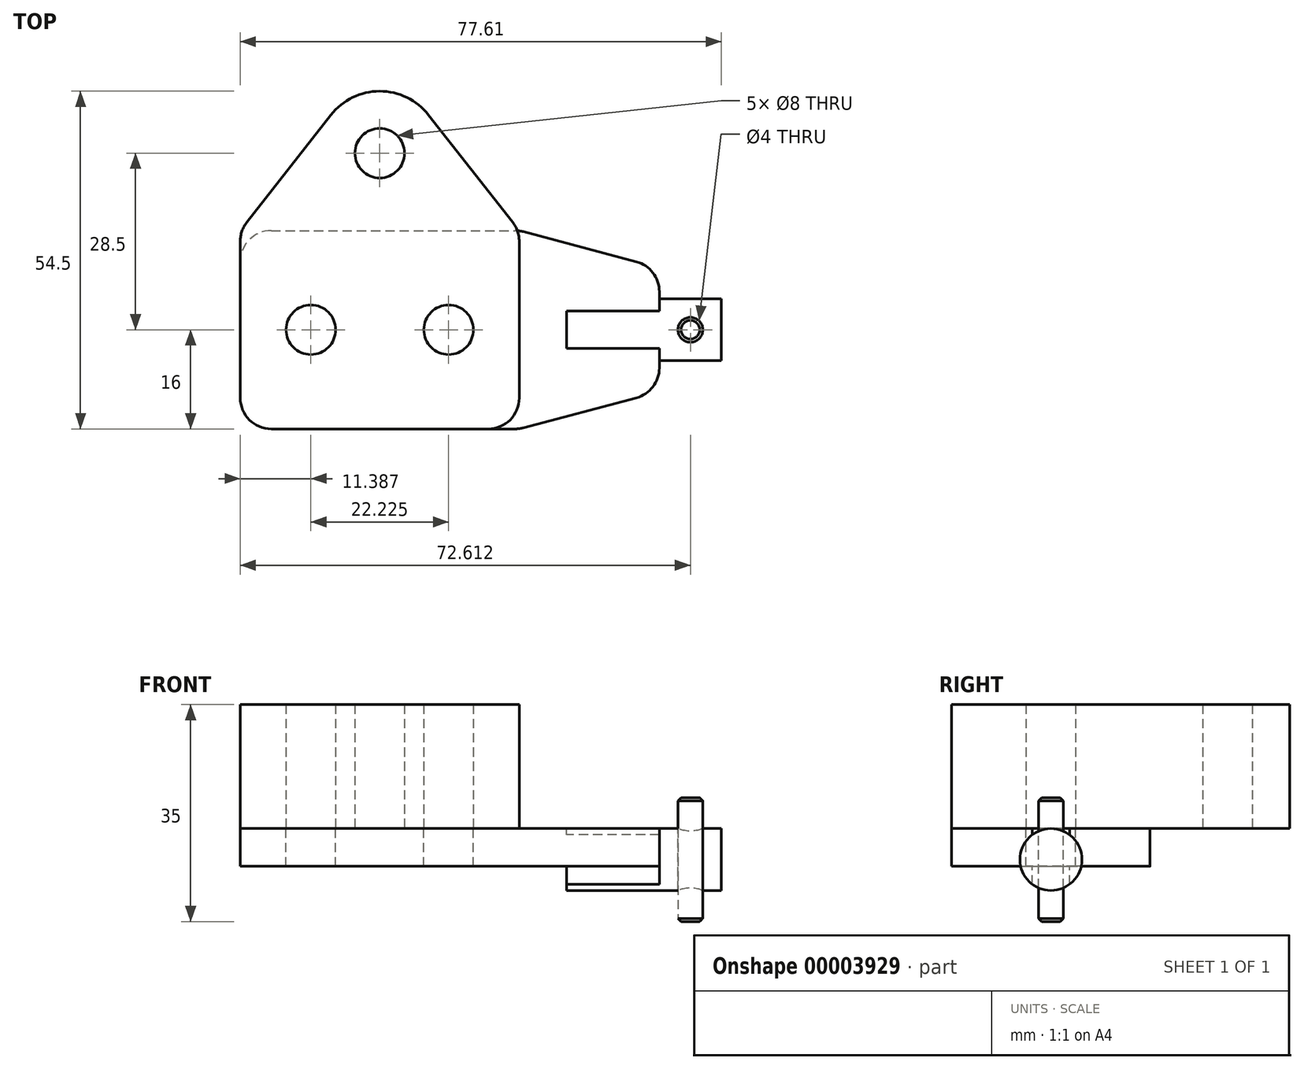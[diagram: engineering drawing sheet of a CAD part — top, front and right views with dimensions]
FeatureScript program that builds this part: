
annotation { "Feature Type Name" : "Feature", "Feature Type Description" : "" }
export const myFeature = defineFeature(function(context is Context, id is Id, definition is map)
    precondition{}
    {
        {
            var Q0;
            Q0=qCreatedBy(makeId("Top.planeOp"),FACE);
            var sketch = newSketch(context, id + "F0", { "sketchPlane" : qUnion([Q0])});
            skCircle(sketch, "E0", {"center": v(-11.11, 0) * mm, "radius": 4 * mm});
            skLineSegment(sketch, "E1", {"start": v(0, -16) * mm, "end": v(-22.5, -16) * mm});
            skLineSegment(sketch, "E2", {"start": v(-22.5, -16) * mm, "end": v(-22.5, 0) * mm});
            skLineSegment(sketch, "E3", {"start": v(-22.5, 0) * mm, "end": v(-22.5, 16) * mm});
            skLineSegment(sketch, "E4", {"start": v(-22.5, 16) * mm, "end": v(0, 16) * mm, "construction": true});
            skCircle(sketch, "E5", {"center": v(0, 28.5) * mm, "radius": 10 * mm});
            skCircle(sketch, "E6", {"center": v(0, 28.5) * mm, "radius": 4 * mm});
            skLineSegment(sketch, "E7", {"start": v(-22.5, 16) * mm, "end": v(-7.87, 34.67) * mm});
            skCircle(sketch, "E8.0.MirrorC", {"center": v(11.11, 0) * mm, "radius": 4 * mm});
            skLineSegment(sketch, "E8.1.MirrorCS", {"start": v(0, -16) * mm, "end": v(22.5, -16) * mm});
            skLineSegment(sketch, "E8.2.MirrorCS", {"start": v(22.5, -16) * mm, "end": v(22.5, 0) * mm});
            skLineSegment(sketch, "E8.3.MirrorCS", {"start": v(22.5, 16) * mm, "end": v(7.87, 34.67) * mm});
            skLineSegment(sketch, "E8.4.MirrorCS", {"start": v(22.5, 0) * mm, "end": v(22.5, 16) * mm});
            skSolve(sketch);
        }
        {
            var Q0;
            Q0=makeQuery(id+"F0.imprint","IMPRINT",FACE,{"disambiguationData":[TD([[makeQuery(id+"F0.imprint","IMPRINT",EDGE,{"derivedFrom":sQuery(id+"F0.wireOp",EDGE,"E0")}),-1.0]])]});
            var Q1;
            Q1=makeQuery(id+"F0.imprint","IMPRINT",FACE,{"disambiguationData":[TD([[makeQuery(id+"F0.imprint","IMPRINT",EDGE,{"derivedFrom":sQuery(id+"F0.wireOp",EDGE,"E6")}),-1.0]])]});
            extrude(context, id + "F1", {"entities" : qUnion([Q0, Q1]), "depth" : 20 * mm});
        }
        {
            var Q0;
            Q0=makeQuery(id+"F1.opExtrude","SWEPT_EDGE",EDGE,{"disambiguationData":[OSD([sQuery(id+"F0.wireOp",EDGE,"E8.3.MirrorCS"),sQuery(id+"F0.wireOp",EDGE,"E8.4.MirrorCS")])]});
            var Q1;
            Q1=makeQuery(id+"F1.opExtrude","SWEPT_EDGE",EDGE,{"disambiguationData":[OSD([sQuery(id+"F0.wireOp",EDGE,"E8.1.MirrorCS"),sQuery(id+"F0.wireOp",EDGE,"E8.2.MirrorCS")])]});
            var Q2;
            Q2=makeQuery(id+"F1.opExtrude","SWEPT_EDGE",EDGE,{"disambiguationData":[OSD([sQuery(id+"F0.wireOp",EDGE,"E1"),sQuery(id+"F0.wireOp",EDGE,"E2")])]});
            var Q3;
            Q3=makeQuery(id+"F1.opExtrude","SWEPT_EDGE",EDGE,{"disambiguationData":[OSD([sQuery(id+"F0.wireOp",EDGE,"E3"),sQuery(id+"F0.wireOp",EDGE,"E7")])]});
            fillet(context, id + "F2", {"entities" : qUnion([Q0, Q1, Q2, Q3]), "radius" : 5 * mm, "tangentPropagation" : true, "allowEdgeOverflow" : false});
        }
        {
            var Q0;
            Q0=qCreatedBy(makeId("Top.planeOp"),FACE);
            var sketch = newSketch(context, id + "F3", { "sketchPlane" : qUnion([Q0])});
            skCircle(sketch, "E9.0", {"center": v(-11.11, 0) * mm, "radius": 4 * mm});
            skCircle(sketch, "E9.1", {"center": v(11.11, 0) * mm, "radius": 4 * mm});
            skLineSegment(sketch, "E10", {"start": v(11.11, 0) * mm, "end": v(45.11, 0) * mm, "construction": true});
            skLineSegment(sketch, "E11", {"start": v(-22.5, 0) * mm, "end": v(-22.5, -16) * mm});
            skLineSegment(sketch, "E12", {"start": v(-22.5, -16) * mm, "end": v(0, -16) * mm});
            skLineSegment(sketch, "E13", {"start": v(0, -16) * mm, "end": v(22.5, -16) * mm});
            skLineSegment(sketch, "E14", {"start": v(45.11, -10) * mm, "end": v(22.5, -16) * mm});
            skLineSegment(sketch, "E15", {"start": v(45.11, -10) * mm, "end": v(45.11, -3) * mm});
            skLineSegment(sketch, "E16", {"start": v(45.11, -3) * mm, "end": v(30.11, -3) * mm});
            skLineSegment(sketch, "E17", {"start": v(30.11, -3) * mm, "end": v(30.11, 0) * mm});
            skLineSegment(sketch, "E18", {"start": v(45.11, -3) * mm, "end": v(45.11, 0) * mm, "construction": true});
            skLineSegment(sketch, "E19.0.MirrorCS", {"start": v(-22.5, 0) * mm, "end": v(-22.5, 16) * mm});
            skLineSegment(sketch, "E20.0.MirrorCS", {"start": v(-22.5, 16) * mm, "end": v(0, 16) * mm});
            skLineSegment(sketch, "E21.0.MirrorCS", {"start": v(0, 16) * mm, "end": v(22.5, 16) * mm});
            skLineSegment(sketch, "E22.0.MirrorCS", {"start": v(45.11, 10) * mm, "end": v(22.5, 16) * mm});
            skLineSegment(sketch, "E23.0.MirrorCS", {"start": v(45.11, 10) * mm, "end": v(45.11, 3) * mm});
            skLineSegment(sketch, "E24.0.MirrorCS", {"start": v(45.11, 3) * mm, "end": v(30.11, 3) * mm});
            skLineSegment(sketch, "E25.0.MirrorCS", {"start": v(30.11, 3) * mm, "end": v(30.11, 0) * mm});
            skSolve(sketch);
        }
        {
            var Q0;
            Q0=makeQuery(id+"F3.imprint","IMPRINT",FACE,{"disambiguationData":[TD([[makeQuery(id+"F3.imprint","IMPRINT",EDGE,{"derivedFrom":sQuery(id+"F3.wireOp",EDGE,"E9.0")}),-1.0]])]});
            extrude(context, id + "F4", {"entities" : qUnion([Q0]), "oppositeDirection" : true, "depth" : 6.1 * mm});
        }
        {
            var Q0;
            Q0=makeQuery(id+"F4.opExtrude","SWEPT_EDGE",EDGE,{"disambiguationData":[OSD([sQuery(id+"F3.wireOp",EDGE,"E11"),sQuery(id+"F3.wireOp",EDGE,"E12")])]});
            var Q1;
            Q1=makeQuery(id+"F4.opExtrude","SWEPT_EDGE",EDGE,{"disambiguationData":[OSD([sQuery(id+"F3.wireOp",EDGE,"E13"),sQuery(id+"F3.wireOp",EDGE,"E14")])]});
            var Q2;
            Q2=makeQuery(id+"F4.opExtrude","SWEPT_EDGE",EDGE,{"disambiguationData":[OSD([sQuery(id+"F3.wireOp",EDGE,"E19.0.MirrorCS"),sQuery(id+"F3.wireOp",EDGE,"E20.0.MirrorCS")])]});
            var Q3;
            Q3=makeQuery(id+"F4.opExtrude","SWEPT_EDGE",EDGE,{"disambiguationData":[OSD([sQuery(id+"F3.wireOp",EDGE,"E21.0.MirrorCS"),sQuery(id+"F3.wireOp",EDGE,"E22.0.MirrorCS")])]});
            var Q4;
            Q4=makeQuery(id+"F4.opExtrude","SWEPT_EDGE",EDGE,{"disambiguationData":[OSD([sQuery(id+"F3.wireOp",EDGE,"E14"),sQuery(id+"F3.wireOp",EDGE,"E15")])]});
            var Q5;
            Q5=makeQuery(id+"F4.opExtrude","SWEPT_EDGE",EDGE,{"disambiguationData":[OSD([sQuery(id+"F3.wireOp",EDGE,"E22.0.MirrorCS"),sQuery(id+"F3.wireOp",EDGE,"E23.0.MirrorCS")])]});
            fillet(context, id + "F5", {"entities" : qUnion([Q0, Q1, Q2, Q3, Q4, Q5]), "radius" : 5 * mm, "tangentPropagation" : true, "allowEdgeOverflow" : false});
        }
        {
            var Q0;
            Q0=makeQuery(id+"F4.opExtrude","SWEPT_FACE",FACE,{"disambiguationData":[OSD([sQuery(id+"F3.wireOp",EDGE,"E17"),sQuery(id+"F3.wireOp",EDGE,"E25.0.MirrorCS")])]});
            cPlane(context, id + "F6", {"entities" : qUnion([Q0]), "cplaneType" : CPlaneType.OFFSET, "offset" : 0 * mm, "width" : 150 * mm, "height" : 150 * mm});
        }
        {
            var Q0;
            Q0=qCreatedBy(id+"F6.planeOp",FACE);
            var sketch = newSketch(context, id + "F7", { "sketchPlane" : qUnion([Q0])});
            skCircle(sketch, "E26", {"center": v(0, -5) * mm, "radius": 5 * mm});
            skLineSegment(sketch, "E27", {"start": v(-3, -1) * mm, "end": v(-3, -9) * mm});
            skLineSegment(sketch, "E28.0.MirrorCS", {"start": v(3, -1) * mm, "end": v(3, -9) * mm});
            skSolve(sketch);
        }
        {
            var Q0;
            {var subQ1=sQuery(id+"F7.wireOp",EDGE,"E27");Q0=makeQuery(id+"F7.imprint","IMPRINT",FACE,{"disambiguationData":[TD([[makeQuery(id+"F7.imprint","IMPRINT",EDGE,{"derivedFrom":subQ1}),1.0]])]});}
            var Q1;
            {var subQ0=sQuery(id+"F7.wireOp",EDGE,"E27");Q1=makeQuery(id+"F7.imprint","IMPRINT",FACE,{"disambiguationData":[TD([[makeQuery(id+"F7.imprint","IMPRINT",EDGE,{"derivedFrom":subQ0}),-1.0]])]});}
            var Q2;
            {var subQ0=sQuery(id+"F7.wireOp",EDGE,"E28.0.MirrorCS");Q2=makeQuery(id+"F7.imprint","IMPRINT",FACE,{"disambiguationData":[TD([[makeQuery(id+"F7.imprint","IMPRINT",EDGE,{"derivedFrom":subQ0}),1.0]])]});}
            extrude(context, id + "F8", {"entities" : qUnion([Q0, Q1, Q2]), "depth" : 25 * mm, "hasSecondDirection" : true, "secondDirectionOppositeDirection" : false, "secondDirectionDepth" : 15 * mm});
        }
        {
            var Q0;
            {var subQ1=sQuery(id+"F7.wireOp",EDGE,"E27");Q0=makeQuery(id+"F7.imprint","IMPRINT",FACE,{"disambiguationData":[TD([[makeQuery(id+"F7.imprint","IMPRINT",EDGE,{"derivedFrom":subQ1}),1.0]])]});}
            extrude(context, id + "F9", {"entities" : qUnion([Q0]), "operationType" : NewBodyOperationType.ADD, "depth" : 25 * mm});
        }
        {
            var Q0;
            Q0=qCreatedBy(makeId("Top.planeOp"),FACE);
            var sketch = newSketch(context, id + "F10", { "sketchPlane" : qUnion([Q0])});
            skLineSegment(sketch, "E29.0", {"start": v(55.11, 5) * mm, "end": v(55.11, -5) * mm, "construction": true});
            skCircle(sketch, "E30", {"center": v(50.11, 0) * mm, "radius": 2 * mm});
            skSolve(sketch);
        }
        {
            var Q0;
            Q0=makeQuery(id+"F10.imprint","IMPRINT",FACE,{"disambiguationData":[TD([[makeQuery(id+"F10.imprint","IMPRINT",EDGE,{"derivedFrom":sQuery(id+"F10.wireOp",EDGE,"E30")}),1.0]])]});
            extrude(context, id + "F11", {"entities" : qUnion([Q0]), "operationType" : NewBodyOperationType.REMOVE, "endBound" : BoundingType.THROUGH_ALL, "oppositeDirection" : true, "depth" : 25 * mm, "hasSecondDirection" : true, "secondDirectionBound" : SecondDirectionBoundingType.THROUGH_ALL, "secondDirectionOppositeDirection" : false, "secondDirectionDepth" : 25 * mm});
        }
        {
            var Q0;
            Q0=makeQuery(id+"F10.imprint","IMPRINT",FACE,{"disambiguationData":[TD([[makeQuery(id+"F10.imprint","IMPRINT",EDGE,{"derivedFrom":sQuery(id+"F10.wireOp",EDGE,"E30")}),1.0]])]});
            extrude(context, id + "F12", {"entities" : qUnion([Q0]), "depth" : 5 * mm, "hasSecondDirection" : true, "secondDirectionOppositeDirection" : true, "secondDirectionDepth" : 15 * mm});
        }
        {
            var Q0;
            Q0=makeQuery(id+"F12.opExtrude","CAP_EDGE",EDGE,{"disambiguationData":[OSD([sQuery(id+"F10.wireOp",EDGE,"E30")])],"isStart":false});
            var Q1;
            Q1=makeQuery(id+"F12.opExtrude","CAP_EDGE",EDGE,{"disambiguationData":[OSD([sQuery(id+"F10.wireOp",EDGE,"E30")])],"isStart":true});
            chamfer(context, id + "F13", {"entities" : qUnion([Q0, Q1]), "width" : 0.5 * mm, "tangentPropagation" : true});
        }
    });
